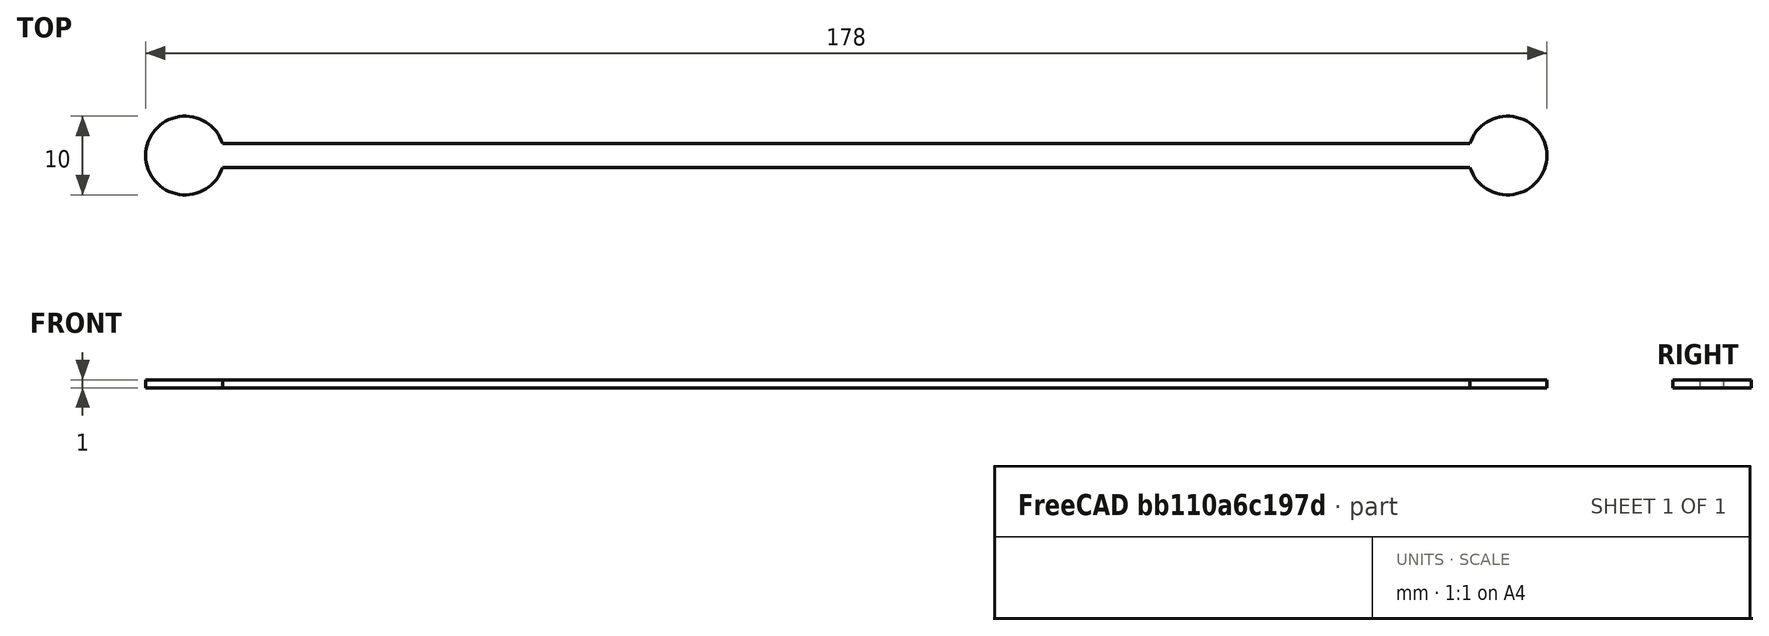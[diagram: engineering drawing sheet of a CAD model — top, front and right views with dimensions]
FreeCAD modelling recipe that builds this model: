
FCSTD DOCUMENT  (FreeCAD 0.19R24276 (Git))
Label: Line_168
License: All rights reserved
LicenseURL: http://en.wikipedia.org/wiki/All_rights_reserved
objects: Sketcher::SketchObject×1, PartDesign::Pad×1, PartDesign::Body×1
note: 4 computed .brp shape members not serialized (recipe doc carries the construction recipe); baked Part::Feature solids carry a one-line shape summary decoded from their .brp

FEATURE [Sketcher::SketchObject] Sketch
  FullyConstrained = false
  MapMode = 5
  Support = -> [XY_Plane]
  sketch-geometry (6):
    g0: ArcOfCircle CenterX=0 CenterY=0 CenterZ=0 NormalX=0 NormalY=0 NormalZ=1 AngleXU=0 Radius=5 StartAngle=0.304693 EndAngle=5.97849
    g1: ArcOfCircle CenterX=168 CenterY=0 CenterZ=0 NormalX=0 NormalY=0 NormalZ=1 AngleXU=0 Radius=5 StartAngle=3.44629 EndAngle=9.12009
    g2: LineSegment StartX=4.7697 StartY=1.5 StartZ=0 EndX=163.23 EndY=1.5 EndZ=0
    g3: LineSegment StartX=168 StartY=1.5 StartZ=0 EndX=168 EndY=-1.5 EndZ=0
    g4: LineSegment StartX=163.23 StartY=-1.5 StartZ=0 EndX=4.7697 EndY=-1.5 EndZ=0
    g5: LineSegment StartX=1.30488 StartY=-1.5 StartZ=0 EndX=1.30488 EndY=1.5 EndZ=0
  constraints (17):
    c: Coincident(g0,g-1)
    c: PointOnObject(g1,g-1)
    c: DistanceX(g-1,g1) = 168
    c: Diameter(g1) = 10
    c: Equal(g1,g0)
    c: Horizontal(g2)
    c: Horizontal(g4)
    c: Vertical(g3)
    c: Vertical(g5)
    c: DistanceY(g3,g3) = 3
    c: Coincident(g0,g2)
    c: Coincident(g4,g0)
    c: Coincident(g2,g1)
    c: Coincident(g4,g1)
    c: Horizontal(g1,g3)
    c: Symmetric(g3,g3,g1)
    c: Horizontal(g1,g3)
FEATURE [PartDesign::Pad] Pad
  Direction = (1,1,1)
  Length = 1
  Length2 = 100
  Profile = -> Sketch
  Type = 0
FEATURE [PartDesign::Body] Body
  Group = -> [Sketch,Pad]
  Origin = -> Origin
  Tip = -> Pad
